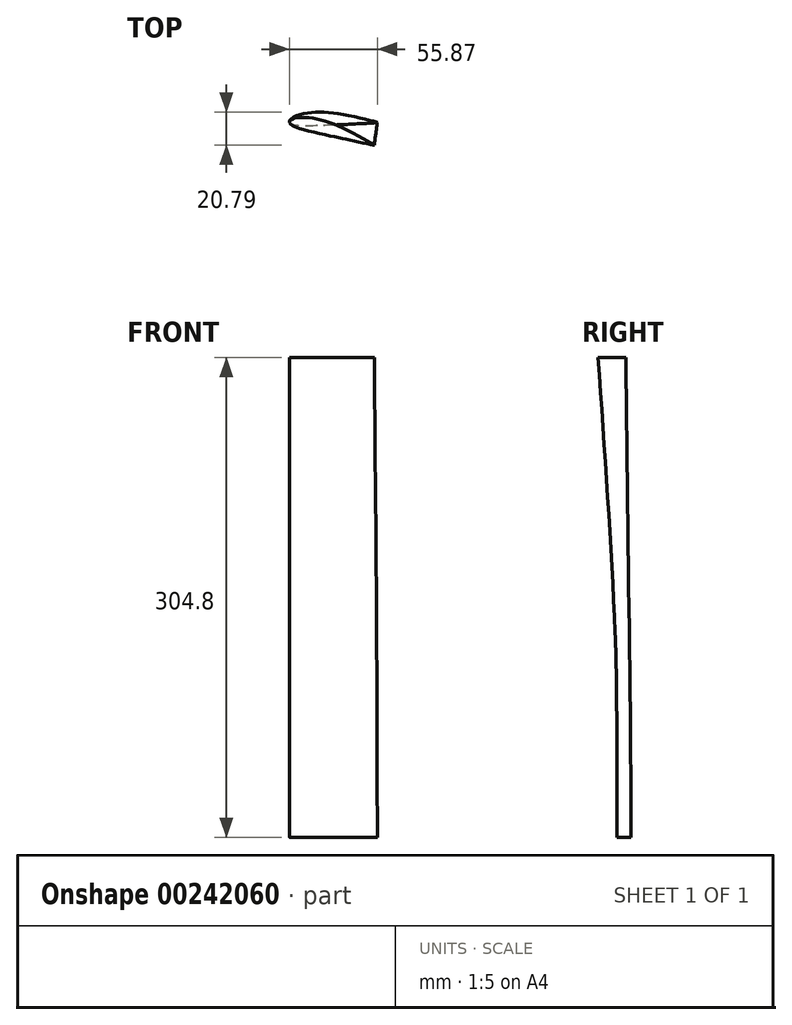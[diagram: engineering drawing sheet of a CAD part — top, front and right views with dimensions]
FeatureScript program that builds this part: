
annotation { "Feature Type Name" : "Feature", "Feature Type Description" : "" }
export const myFeature = defineFeature(function(context is Context, id is Id, definition is map)
    precondition{}
    {
        {
            var Q0;
            Q0=qCreatedBy(makeId("Top.planeOp"),FACE);
            var sketch = newSketch(context, id + "F0", { "sketchPlane" : qUnion([Q0])});
            skFitSpline(sketch, "E0", {"points": [v(0, 0) * mm, v(1.17, 2.35) * mm, v(8.63, 5.45) * mm, v(20.02, 6.45) * mm, v(35.72, 4.8) * mm, v(53.51, 0.65) * mm, v(55.8, 0) * mm, v(51.98, -0.43) * mm, v(39.19, -1.13) * mm, v(27.69, -1.67) * mm, v(8.1, -2.32) * mm, v(2.66, -1.63) * mm, v(0, 0) * mm]});
            skSolve(sketch);
        }
        {
            var Q0;
            Q0=qCreatedBy(makeId("Top.planeOp"),FACE);
            cPlane(context, id + "F1", {"entities" : qUnion([Q0]), "cplaneType" : CPlaneType.OFFSET, "offset" : 304.8 * mm, "width" : 152.4 * mm, "height" : 152.4 * mm});
        }
        {
            var Q0;
            Q0=qCreatedBy(id+"F1.planeOp",FACE);
            var sketch = newSketch(context, id + "F2", { "sketchPlane" : qUnion([Q0])});
            skFitSpline(sketch, "E1", {"points": [v(-0.02, 0.14) * mm, v(1.71, 2.1) * mm, v(9.72, 3.18) * mm, v(20.99, 1.19) * mm, v(35.73, -4.47) * mm, v(51.84, -13.08) * mm, v(53.88, -14.3) * mm, v(50.08, -13.73) * mm, v(37.54, -11.09) * mm, v(26.3, -8.64) * mm, v(7.2, -4.2) * mm, v(2.12, -2.12) * mm, v(-0.02, 0.14) * mm]});
            skSolve(sketch);
        }
        {
            var Q0;
            Q0 = qSketchRegion(id + "F0", true);
            var Q1;
            Q1 = qSketchRegion(id + "F2", true);
            loft(context, id + "F3", {"startCondition" : LoftEndDerivativeType.NORMAL_TO_PROFILE, "startMagnitude" : 1, "sheetProfilesArray" : [{ "sheetProfileEntities" : qUnion([Q0]) }, { "sheetProfileEntities" : qUnion([Q1]) }]});
        }
    });
